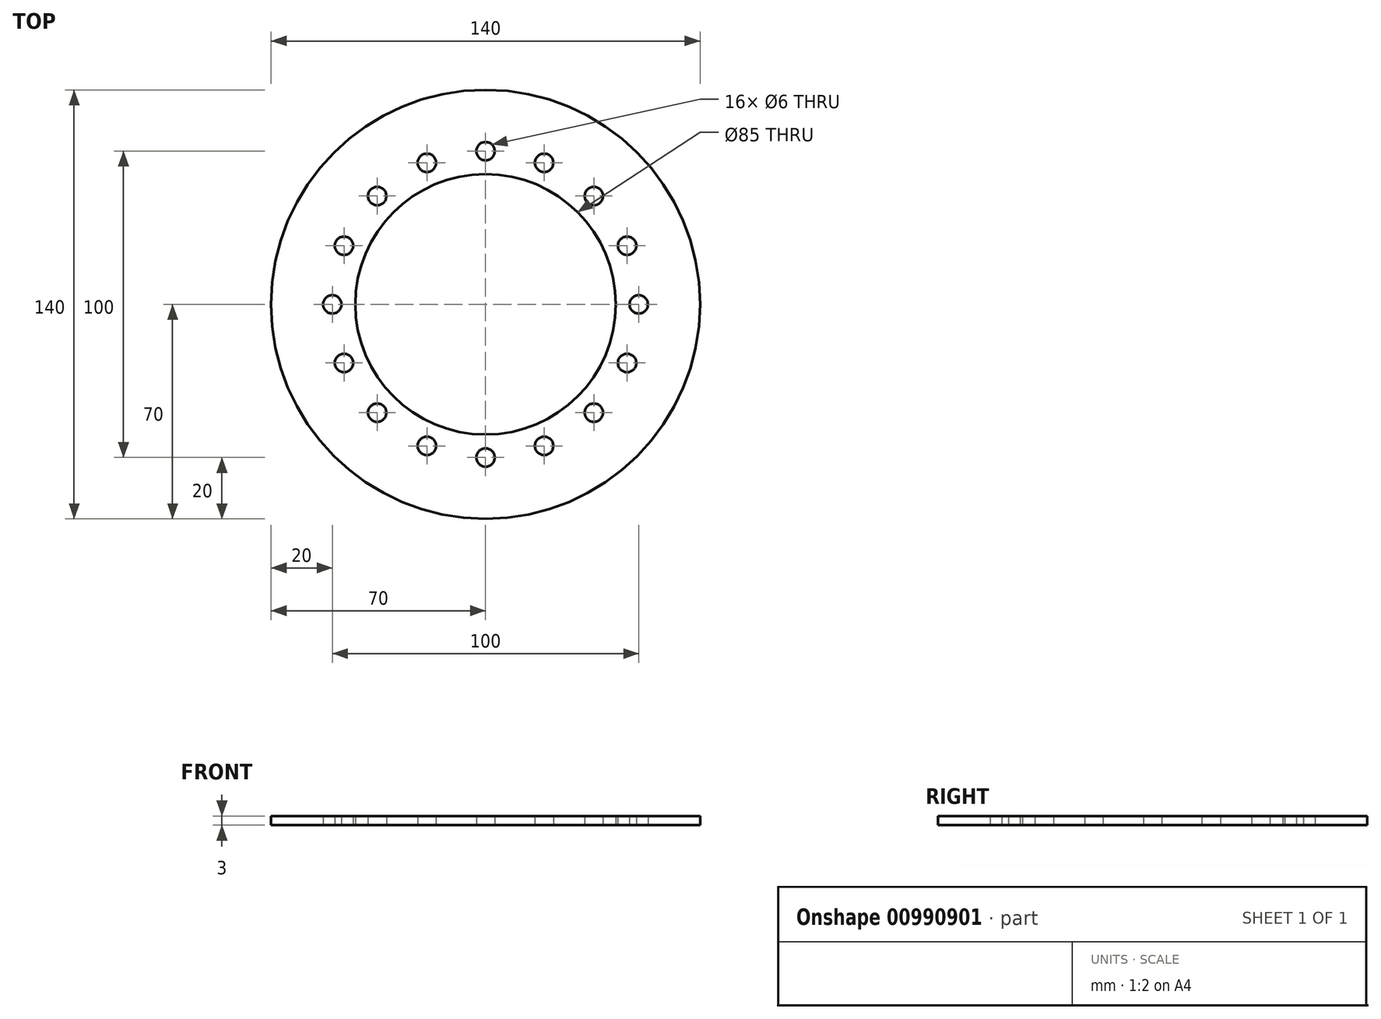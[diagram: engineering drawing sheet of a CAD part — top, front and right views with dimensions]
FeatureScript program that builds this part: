
annotation { "Feature Type Name" : "Feature", "Feature Type Description" : "" }
export const myFeature = defineFeature(function(context is Context, id is Id, definition is map)
    precondition{}
    {
        {
            var Q0;
            Q0=qCreatedBy(makeId("Top.planeOp"),FACE);
            var sketch = newSketch(context, id + "F0", { "sketchPlane" : qUnion([Q0])});
            skCircle(sketch, "E0", {"center": v(0, 0) * mm, "radius": 70 * mm});
            skCircle(sketch, "E1", {"center": v(0, 0) * mm, "radius": 50 * mm, "construction": true});
            skCircle(sketch, "E2", {"center": v(0, 50) * mm, "radius": 3 * mm});
            skCircle(sketch, "E3.1.0", {"center": v(-19.13, 46.2) * mm, "radius": 3 * mm});
            skCircle(sketch, "E3.2.0", {"center": v(-35.36, 35.36) * mm, "radius": 3 * mm});
            skCircle(sketch, "E3.3.0", {"center": v(-46.2, 19.13) * mm, "radius": 3 * mm});
            skCircle(sketch, "E3.4.0", {"center": v(-50, 0) * mm, "radius": 3 * mm});
            skCircle(sketch, "E3.5.0", {"center": v(-46.2, -19.13) * mm, "radius": 3 * mm});
            skCircle(sketch, "E3.6.0", {"center": v(-35.36, -35.36) * mm, "radius": 3 * mm});
            skCircle(sketch, "E3.7.0", {"center": v(-19.13, -46.2) * mm, "radius": 3 * mm});
            skCircle(sketch, "E3.8.0", {"center": v(0, -50) * mm, "radius": 3 * mm});
            skCircle(sketch, "E3.9.0", {"center": v(19.13, -46.2) * mm, "radius": 3 * mm});
            skCircle(sketch, "E3.10.0", {"center": v(35.36, -35.36) * mm, "radius": 3 * mm});
            skCircle(sketch, "E3.11.0", {"center": v(46.2, -19.13) * mm, "radius": 3 * mm});
            skCircle(sketch, "E3.12.0", {"center": v(50, 0) * mm, "radius": 3 * mm});
            skCircle(sketch, "E3.13.0", {"center": v(46.2, 19.13) * mm, "radius": 3 * mm});
            skCircle(sketch, "E3.14.0", {"center": v(35.36, 35.36) * mm, "radius": 3 * mm});
            skCircle(sketch, "E3.15.0", {"center": v(19.13, 46.2) * mm, "radius": 3 * mm});
            skCircle(sketch, "E4", {"center": v(0, 0) * mm, "radius": 42.5 * mm});
            skSolve(sketch);
        }
        {
            var Q0;
            Q0=qSketchRegion(id+"F0",true);
            extrude(context, id + "F1", {"entities" : qUnion([Q0]), "depth" : 3 * mm, "offsetDistance" : 25 * mm});
        }
    });
